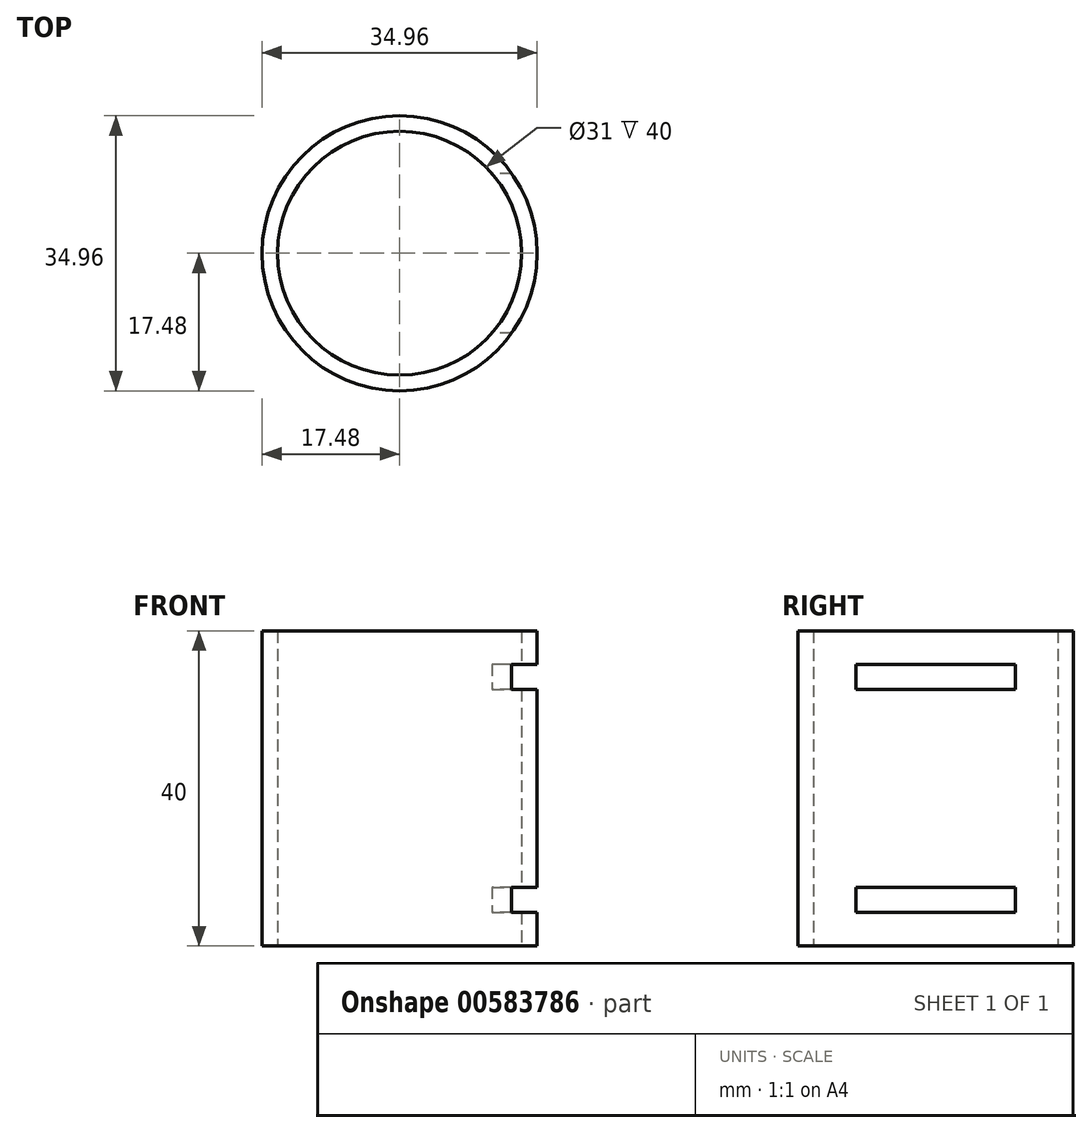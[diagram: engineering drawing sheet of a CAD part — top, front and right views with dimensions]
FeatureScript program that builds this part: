
annotation { "Feature Type Name" : "Feature", "Feature Type Description" : "" }
export const myFeature = defineFeature(function(context is Context, id is Id, definition is map)
    precondition{}
    {
        {
            var Q0;
            Q0=qCreatedBy(makeId("Top.planeOp"),FACE);
            var sketch = newSketch(context, id + "F0", { "sketchPlane" : qUnion([Q0])});
            skCircle(sketch, "E0", {"center": v(0, 0) * mm, "radius": 17.48 * mm});
            skCircle(sketch, "E1", {"center": v(0, 0) * mm, "radius": 15.5 * mm});
            skSolve(sketch);
        }
        {
            var Q0;
            Q0=makeQuery(id+"F0.imprint","IMPRINT",FACE,{"disambiguationData":[TD([[makeQuery(id+"F0.imprint","IMPRINT",EDGE,{"derivedFrom":sQuery(id+"F0.wireOp",EDGE,"E0")}),1.0]])]});
            extrude(context, id + "F1", {"entities" : qUnion([Q0]), "endBound" : BoundingType.SYMMETRIC, "depth" : 40 * mm, "offsetDistance" : 25 * mm});
        }
        {
            var Q0;
            Q0=qCreatedBy(makeId("Right.planeOp"),FACE);
            var sketch = newSketch(context, id + "F2", { "sketchPlane" : qUnion([Q0])});
            skLineSegment(sketch, "E2.bottom", {"start": v(10.13, 12.54) * mm, "end": v(-10.13, 12.54) * mm});
            skLineSegment(sketch, "E2.top", {"start": v(10.13, 15.77) * mm, "end": v(-10.13, 15.77) * mm});
            skLineSegment(sketch, "E2.left", {"start": v(10.13, 12.54) * mm, "end": v(10.13, 15.77) * mm});
            skLineSegment(sketch, "E2.right", {"start": v(-10.13, 12.54) * mm, "end": v(-10.13, 15.77) * mm});
            skPoint(sketch, "E2.middle", {"position": v(0, 14.16) * mm});
            skLineSegment(sketch, "E3.MirrorCS", {"start": v(10.13, -12.54) * mm, "end": v(10.13, -15.77) * mm});
            skPoint(sketch, "E4.MirrorP", {"position": v(0, -14.16) * mm});
            skLineSegment(sketch, "E5.MirrorCS", {"start": v(10.13, -12.54) * mm, "end": v(-10.13, -12.54) * mm});
            skLineSegment(sketch, "E6.MirrorCS", {"start": v(-10.13, -12.54) * mm, "end": v(-10.13, -15.77) * mm});
            skLineSegment(sketch, "E7.MirrorCS", {"start": v(10.13, -15.77) * mm, "end": v(-10.13, -15.77) * mm});
            skSolve(sketch);
        }
        {
            var Q0;
            Q0=makeQuery(id+"F2.imprint","IMPRINT",FACE,{"disambiguationData":[TD([[makeQuery(id+"F2.imprint","IMPRINT",EDGE,{"derivedFrom":sQuery(id+"F2.wireOp",EDGE,"E2.bottom")}),-1.0]])]});
            var Q1;
            Q1=makeQuery(id+"F2.imprint","IMPRINT",FACE,{"disambiguationData":[TD([[makeQuery(id+"F2.imprint","IMPRINT",EDGE,{"derivedFrom":sQuery(id+"F2.wireOp",EDGE,"E3.MirrorCS")}),-1.0]])]});
            extrude(context, id + "F3", {"entities" : qUnion([Q0, Q1]), "operationType" : NewBodyOperationType.REMOVE, "depth" : 25 * mm, "offsetDistance" : 25 * mm});
        }
    });
